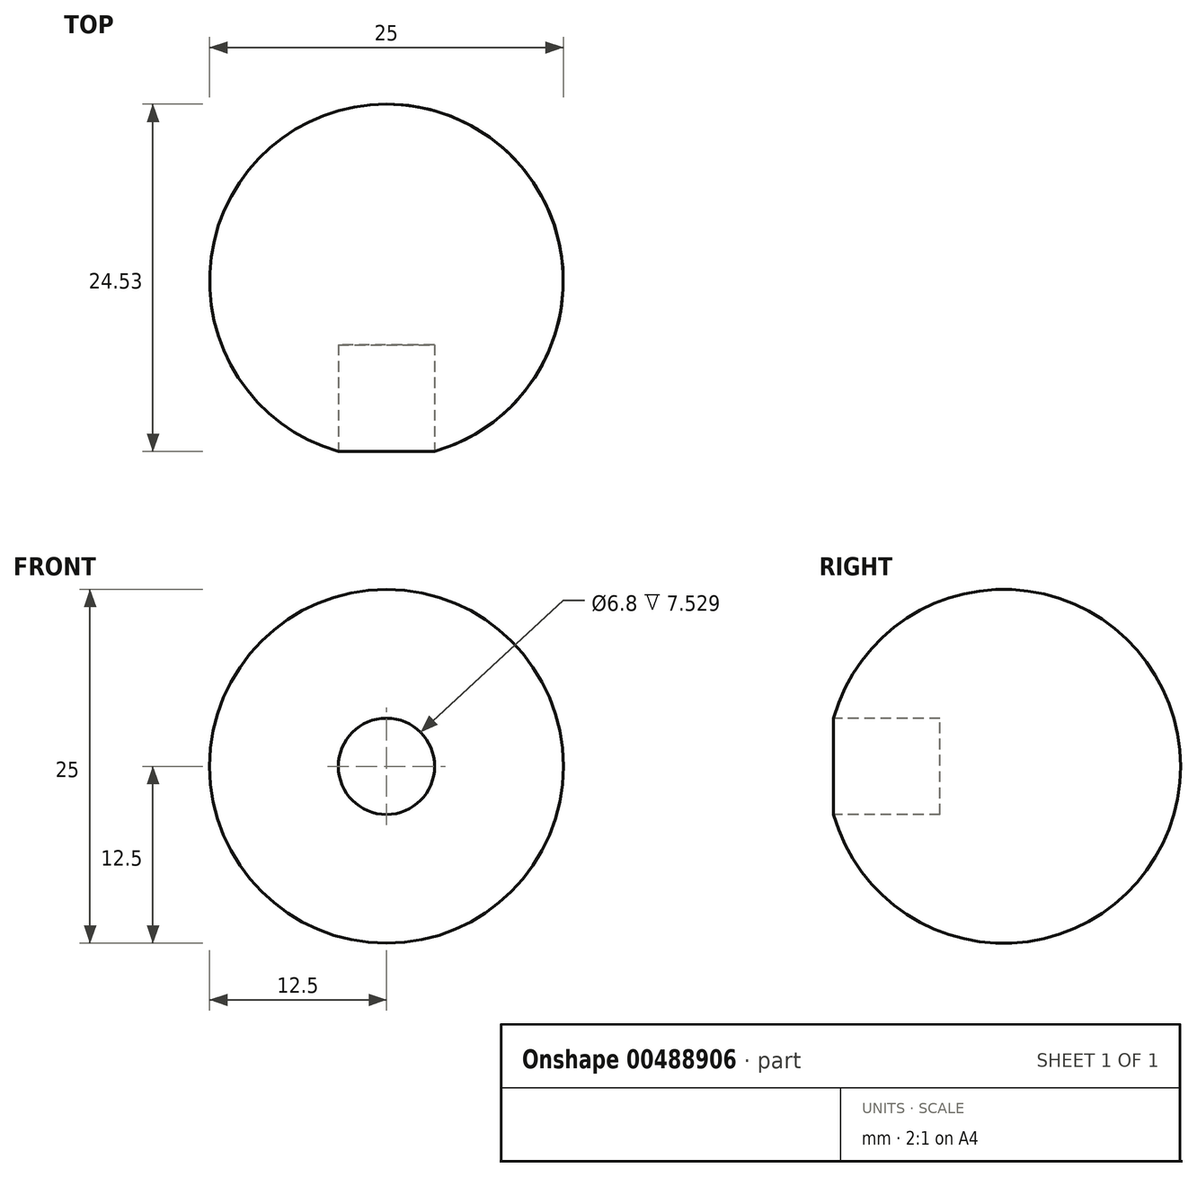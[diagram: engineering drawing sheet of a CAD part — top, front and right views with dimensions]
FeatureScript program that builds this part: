
annotation { "Feature Type Name" : "Feature", "Feature Type Description" : "" }
export const myFeature = defineFeature(function(context is Context, id is Id, definition is map)
    precondition{}
    {
        {
            var Q0;
            Q0=qCreatedBy(makeId("Top.planeOp"),FACE);
            var sketch = newSketch(context, id + "F0", { "sketchPlane" : qUnion([Q0])});
            skLineSegment(sketch, "E0", {"start": v(0, 0) * mm, "end": v(0, 12.5) * mm});
            skArc(sketch, "E1", {"start": v(0, 12.5) * mm, "mid": v(12.38, 1.72) * mm, "end": v(3.4, -12.03) * mm});
            skLineSegment(sketch, "E2", {"start": v(0, 0) * mm, "end": v(0, -4.5) * mm});
            skLineSegment(sketch, "E3.bottom", {"start": v(0, -4.5) * mm, "end": v(3.4, -4.5) * mm});
            skLineSegment(sketch, "E3.right", {"start": v(3.4, -4.5) * mm, "end": v(3.4, -12.03) * mm});
            skSolve(sketch);
        }
        {
            var Q0;
            Q0=makeQuery(id+"F0.imprint","IMPRINT",FACE,{"disambiguationData":[TD([[makeQuery(id+"F0.imprint","IMPRINT",EDGE,{"derivedFrom":sQuery(id+"F0.wireOp",EDGE,"E0")}),-1.0]])]});
            var Q1;
            Q1=sQuery(id+"F0.wireOp",EDGE,"E0");
            revolve(context, id + "F1", {"entities" : qUnion([Q0]), "axis" : qUnion([Q1]), "revolveType" : RevolveType.FULL});
        }
    });
